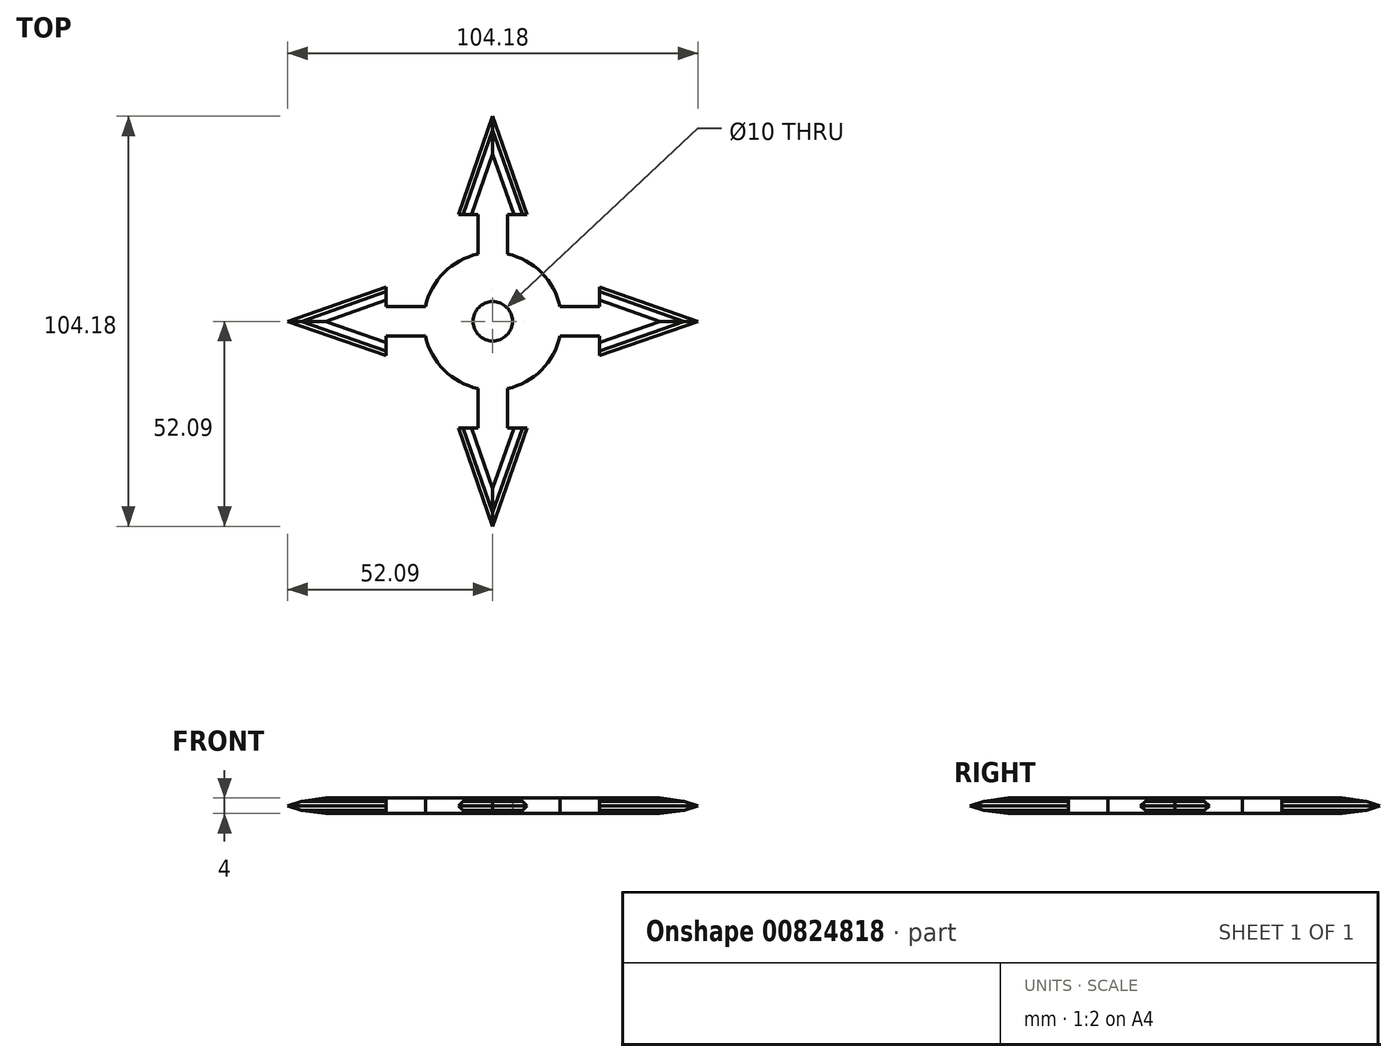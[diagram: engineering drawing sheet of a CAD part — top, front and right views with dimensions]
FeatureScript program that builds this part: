
annotation { "Feature Type Name" : "Feature", "Feature Type Description" : "" }
export const myFeature = defineFeature(function(context is Context, id is Id, definition is map)
    precondition{}
    {
        {
            var Q0;
            Q0=qCreatedBy(makeId("Top.planeOp"),FACE);
            var sketch = newSketch(context, id + "F0", { "sketchPlane" : qUnion([Q0])});
            skCircle(sketch, "E0", {"center": v(0, 0) * mm, "radius": 5 * mm});
            skCircle(sketch, "E1", {"center": v(0, 0) * mm, "radius": 17.5 * mm});
            skLineSegment(sketch, "E2", {"start": v(-3.75, 17.1) * mm, "end": v(-3.75, 27.1) * mm});
            skLineSegment(sketch, "E3", {"start": v(-3.75, 27.1) * mm, "end": v(3.75, 27.1) * mm});
            skLineSegment(sketch, "E4", {"start": v(3.75, 27.1) * mm, "end": v(3.75, 17.1) * mm});
            skLineSegment(sketch, "E5", {"start": v(17.1, 3.75) * mm, "end": v(27.1, 3.75) * mm});
            skLineSegment(sketch, "E6", {"start": v(27.1, 3.75) * mm, "end": v(27.1, -3.75) * mm});
            skLineSegment(sketch, "E7", {"start": v(27.1, -3.75) * mm, "end": v(17.1, -3.75) * mm});
            skLineSegment(sketch, "E8", {"start": v(3.75, -17.1) * mm, "end": v(3.75, -27.1) * mm});
            skLineSegment(sketch, "E9", {"start": v(3.75, -27.1) * mm, "end": v(-3.75, -27.1) * mm});
            skLineSegment(sketch, "E10", {"start": v(-3.75, -27.1) * mm, "end": v(-3.75, -17.1) * mm});
            skLineSegment(sketch, "E11", {"start": v(-17.1, 3.75) * mm, "end": v(-27.1, 3.75) * mm});
            skLineSegment(sketch, "E12", {"start": v(-27.1, 3.75) * mm, "end": v(-27.1, -3.75) * mm});
            skLineSegment(sketch, "E13", {"start": v(-27.1, -3.75) * mm, "end": v(-17.1, -3.75) * mm});
            skLineSegment(sketch, "E14", {"start": v(-27.1, 3.75) * mm, "end": v(-27.1, 8.75) * mm});
            skLineSegment(sketch, "E15", {"start": v(-27.1, 8.75) * mm, "end": v(-52.1, 0) * mm});
            skLineSegment(sketch, "E16", {"start": v(-52.1, 0) * mm, "end": v(-27.1, -8.75) * mm});
            skLineSegment(sketch, "E17", {"start": v(-27.1, -8.75) * mm, "end": v(-27.1, -3.75) * mm});
            skLineSegment(sketch, "E18", {"start": v(-3.75, 27.1) * mm, "end": v(-8.75, 27.1) * mm});
            skLineSegment(sketch, "E19", {"start": v(-8.75, 27.1) * mm, "end": v(0, 52.1) * mm});
            skLineSegment(sketch, "E20", {"start": v(0, 52.1) * mm, "end": v(8.75, 27.1) * mm});
            skLineSegment(sketch, "E21", {"start": v(8.75, 27.1) * mm, "end": v(3.75, 27.1) * mm});
            skLineSegment(sketch, "E22", {"start": v(27.1, 3.75) * mm, "end": v(27.1, 8.75) * mm});
            skLineSegment(sketch, "E23", {"start": v(27.1, 8.75) * mm, "end": v(52.1, 0) * mm});
            skLineSegment(sketch, "E24", {"start": v(52.1, 0) * mm, "end": v(27.1, -8.75) * mm});
            skLineSegment(sketch, "E25", {"start": v(27.1, -8.75) * mm, "end": v(27.1, -3.75) * mm});
            skLineSegment(sketch, "E26", {"start": v(3.75, -27.1) * mm, "end": v(8.75, -27.1) * mm});
            skLineSegment(sketch, "E27", {"start": v(8.75, -27.1) * mm, "end": v(0, -52.1) * mm});
            skLineSegment(sketch, "E28", {"start": v(0, -52.1) * mm, "end": v(-8.75, -27.1) * mm});
            skLineSegment(sketch, "E29", {"start": v(-8.75, -27.1) * mm, "end": v(-3.75, -27.1) * mm});
            skSolve(sketch);
        }
        {
            var Q0;
            Q0=makeQuery(id+"F0.imprint","IMPRINT",FACE,{"disambiguationData":[TD([[makeQuery(id+"F0.imprint","IMPRINT",EDGE,{"derivedFrom":sQuery(id+"F0.wireOp",EDGE,"E0")}),-1.0]])]});
            var Q1;
            {var subQ0=sQuery(id+"F0.wireOp",EDGE,"E11");Q1=makeQuery(id+"F0.imprint","IMPRINT",FACE,{"disambiguationData":[TD([[makeQuery(id+"F0.imprint","IMPRINT",EDGE,{"derivedFrom":subQ0}),1.0]])]});}
            var Q2;
            Q2=makeQuery(id+"F0.imprint","IMPRINT",FACE,{"disambiguationData":[TD([[makeQuery(id+"F0.imprint","IMPRINT",EDGE,{"derivedFrom":sQuery(id+"F0.wireOp",EDGE,"E12")}),-1.0]])]});
            var Q3;
            {var subQ0=sQuery(id+"F0.wireOp",EDGE,"E2");Q3=makeQuery(id+"F0.imprint","IMPRINT",FACE,{"disambiguationData":[TD([[makeQuery(id+"F0.imprint","IMPRINT",EDGE,{"derivedFrom":subQ0}),-1.0]])]});}
            var Q4;
            Q4=makeQuery(id+"F0.imprint","IMPRINT",FACE,{"disambiguationData":[TD([[makeQuery(id+"F0.imprint","IMPRINT",EDGE,{"derivedFrom":sQuery(id+"F0.wireOp",EDGE,"E3")}),1.0]])]});
            var Q5;
            Q5=makeQuery(id+"F0.imprint","IMPRINT",FACE,{"disambiguationData":[TD([[makeQuery(id+"F0.imprint","IMPRINT",EDGE,{"derivedFrom":sQuery(id+"F0.wireOp",EDGE,"E6")}),1.0]])]});
            var Q6;
            Q6=makeQuery(id+"F0.imprint","IMPRINT",FACE,{"disambiguationData":[TD([[makeQuery(id+"F0.imprint","IMPRINT",EDGE,{"derivedFrom":sQuery(id+"F0.wireOp",EDGE,"E9")}),1.0]])]});
            var Q7;
            {var subQ0=sQuery(id+"F0.wireOp",EDGE,"E8");Q7=makeQuery(id+"F0.imprint","IMPRINT",FACE,{"disambiguationData":[TD([[makeQuery(id+"F0.imprint","IMPRINT",EDGE,{"derivedFrom":subQ0}),-1.0]])]});}
            var Q8;
            {var subQ0=sQuery(id+"F0.wireOp",EDGE,"E5");Q8=makeQuery(id+"F0.imprint","IMPRINT",FACE,{"disambiguationData":[TD([[makeQuery(id+"F0.imprint","IMPRINT",EDGE,{"derivedFrom":subQ0}),-1.0]])]});}
            extrude(context, id + "F1", {"entities" : qUnion([Q0, Q1, Q2, Q3, Q4, Q5, Q6, Q7, Q8]), "endBound" : BoundingType.SYMMETRIC, "depth" : 4 * mm, "offsetDistance" : 25 * mm});
        }
        {
            var Q0;
            Q0=makeQuery(id+"F1.opExtrude","CAP_EDGE",EDGE,{"disambiguationData":[OSD([sQuery(id+"F0.wireOp",EDGE,"E27")])],"isStart":false});
            var Q1;
            Q1=makeQuery(id+"F1.opExtrude","CAP_EDGE",EDGE,{"disambiguationData":[OSD([sQuery(id+"F0.wireOp",EDGE,"E28")])],"isStart":false});
            var Q2;
            Q2=makeQuery(id+"F1.opExtrude","CAP_EDGE",EDGE,{"disambiguationData":[OSD([sQuery(id+"F0.wireOp",EDGE,"E27")])],"isStart":true});
            var Q3;
            Q3=makeQuery(id+"F1.opExtrude","CAP_EDGE",EDGE,{"disambiguationData":[OSD([sQuery(id+"F0.wireOp",EDGE,"E28")])],"isStart":true});
            var Q4;
            Q4=makeQuery(id+"F1.opExtrude","CAP_EDGE",EDGE,{"disambiguationData":[OSD([sQuery(id+"F0.wireOp",EDGE,"E24")])],"isStart":true});
            var Q5;
            Q5=makeQuery(id+"F1.opExtrude","CAP_EDGE",EDGE,{"disambiguationData":[OSD([sQuery(id+"F0.wireOp",EDGE,"E24")])],"isStart":false});
            var Q6;
            Q6=makeQuery(id+"F1.opExtrude","CAP_EDGE",EDGE,{"disambiguationData":[OSD([sQuery(id+"F0.wireOp",EDGE,"E23")])],"isStart":false});
            var Q7;
            Q7=makeQuery(id+"F1.opExtrude","CAP_EDGE",EDGE,{"disambiguationData":[OSD([sQuery(id+"F0.wireOp",EDGE,"E16")])],"isStart":false});
            var Q8;
            Q8=makeQuery(id+"F1.opExtrude","CAP_EDGE",EDGE,{"disambiguationData":[OSD([sQuery(id+"F0.wireOp",EDGE,"E16")])],"isStart":true});
            var Q9;
            Q9=makeQuery(id+"F1.opExtrude","CAP_EDGE",EDGE,{"disambiguationData":[OSD([sQuery(id+"F0.wireOp",EDGE,"E19")])],"isStart":false});
            var Q10;
            Q10=makeQuery(id+"F1.opExtrude","CAP_EDGE",EDGE,{"disambiguationData":[OSD([sQuery(id+"F0.wireOp",EDGE,"E20")])],"isStart":false});
            var Q11;
            Q11=makeQuery(id+"F1.opExtrude","CAP_EDGE",EDGE,{"disambiguationData":[OSD([sQuery(id+"F0.wireOp",EDGE,"E23")])],"isStart":true});
            var Q12;
            Q12=makeQuery(id+"F1.opExtrude","CAP_EDGE",EDGE,{"disambiguationData":[OSD([sQuery(id+"F0.wireOp",EDGE,"E20")])],"isStart":true});
            var Q13;
            Q13=makeQuery(id+"F1.opExtrude","CAP_EDGE",EDGE,{"disambiguationData":[OSD([sQuery(id+"F0.wireOp",EDGE,"E15")])],"isStart":false});
            var Q14;
            Q14=makeQuery(id+"F1.opExtrude","CAP_EDGE",EDGE,{"disambiguationData":[OSD([sQuery(id+"F0.wireOp",EDGE,"E15")])],"isStart":true});
            var Q15;
            Q15=makeQuery(id+"F1.opExtrude","CAP_EDGE",EDGE,{"disambiguationData":[OSD([sQuery(id+"F0.wireOp",EDGE,"E19")])],"isStart":true});
            chamfer(context, id + "F2", {"entities" : qUnion([Q0, Q1, Q2, Q3, Q4, Q5, Q6, Q7, Q8, Q9, Q10, Q11, Q12, Q13, Q14, Q15]), "width" : 2 * mm, "tangentPropagation" : true});
        }
        {
            var Q0;
            {var subQ0=sQuery(id+"F0.wireOp",EDGE,"E27");Q0=makeQuery(id+"F2.opChamfer","BLEND_EDGE",EDGE,{"blendedFrom":[makeQuery(id+"F1.opExtrude","CAP_EDGE",EDGE,{"disambiguationData":[OSD([subQ0])],"isStart":false}),makeQuery(id+"F1.opExtrude","CAP_FACE",FACE,{"disambiguationData":[OSD([sQuery(id+"F0.wireOp",EDGE,"E0"),sQuery(id+"F0.wireOp",EDGE,"E1"),sQuery(id+"F0.wireOp",EDGE,"E2"),sQuery(id+"F0.wireOp",EDGE,"E4"),sQuery(id+"F0.wireOp",EDGE,"E5"),sQuery(id+"F0.wireOp",EDGE,"E7"),sQuery(id+"F0.wireOp",EDGE,"E8"),sQuery(id+"F0.wireOp",EDGE,"E10"),sQuery(id+"F0.wireOp",EDGE,"E11"),sQuery(id+"F0.wireOp",EDGE,"E13"),sQuery(id+"F0.wireOp",EDGE,"E14"),sQuery(id+"F0.wireOp",EDGE,"E15"),sQuery(id+"F0.wireOp",EDGE,"E16"),sQuery(id+"F0.wireOp",EDGE,"E17"),sQuery(id+"F0.wireOp",EDGE,"E18"),sQuery(id+"F0.wireOp",EDGE,"E19"),sQuery(id+"F0.wireOp",EDGE,"E20"),sQuery(id+"F0.wireOp",EDGE,"E21"),sQuery(id+"F0.wireOp",EDGE,"E22"),sQuery(id+"F0.wireOp",EDGE,"E23"),sQuery(id+"F0.wireOp",EDGE,"E24"),sQuery(id+"F0.wireOp",EDGE,"E25"),sQuery(id+"F0.wireOp",EDGE,"E26"),subQ0,sQuery(id+"F0.wireOp",EDGE,"E28"),sQuery(id+"F0.wireOp",EDGE,"E29")])],"isStart":false})],"blendedInto":[makeQuery(id+"F1.opExtrude","CAP_FACE",FACE,{"disambiguationData":[OSD([sQuery(id+"F0.wireOp",EDGE,"E0"),sQuery(id+"F0.wireOp",EDGE,"E1"),sQuery(id+"F0.wireOp",EDGE,"E2"),sQuery(id+"F0.wireOp",EDGE,"E4"),sQuery(id+"F0.wireOp",EDGE,"E5"),sQuery(id+"F0.wireOp",EDGE,"E7"),sQuery(id+"F0.wireOp",EDGE,"E8"),sQuery(id+"F0.wireOp",EDGE,"E10"),sQuery(id+"F0.wireOp",EDGE,"E11"),sQuery(id+"F0.wireOp",EDGE,"E13"),sQuery(id+"F0.wireOp",EDGE,"E14"),sQuery(id+"F0.wireOp",EDGE,"E15"),sQuery(id+"F0.wireOp",EDGE,"E16"),sQuery(id+"F0.wireOp",EDGE,"E17"),sQuery(id+"F0.wireOp",EDGE,"E18"),sQuery(id+"F0.wireOp",EDGE,"E19"),sQuery(id+"F0.wireOp",EDGE,"E20"),sQuery(id+"F0.wireOp",EDGE,"E21"),sQuery(id+"F0.wireOp",EDGE,"E22"),sQuery(id+"F0.wireOp",EDGE,"E23"),sQuery(id+"F0.wireOp",EDGE,"E24"),sQuery(id+"F0.wireOp",EDGE,"E25"),sQuery(id+"F0.wireOp",EDGE,"E26"),subQ0,sQuery(id+"F0.wireOp",EDGE,"E28"),sQuery(id+"F0.wireOp",EDGE,"E29")])],"isStart":false})]});}
            var Q1;
            {var subQ0=sQuery(id+"F0.wireOp",EDGE,"E28");Q1=makeQuery(id+"F2.opChamfer","BLEND_EDGE",EDGE,{"blendedFrom":[makeQuery(id+"F1.opExtrude","CAP_EDGE",EDGE,{"disambiguationData":[OSD([subQ0])],"isStart":false}),makeQuery(id+"F1.opExtrude","CAP_FACE",FACE,{"disambiguationData":[OSD([sQuery(id+"F0.wireOp",EDGE,"E0"),sQuery(id+"F0.wireOp",EDGE,"E1"),sQuery(id+"F0.wireOp",EDGE,"E2"),sQuery(id+"F0.wireOp",EDGE,"E4"),sQuery(id+"F0.wireOp",EDGE,"E5"),sQuery(id+"F0.wireOp",EDGE,"E7"),sQuery(id+"F0.wireOp",EDGE,"E8"),sQuery(id+"F0.wireOp",EDGE,"E10"),sQuery(id+"F0.wireOp",EDGE,"E11"),sQuery(id+"F0.wireOp",EDGE,"E13"),sQuery(id+"F0.wireOp",EDGE,"E14"),sQuery(id+"F0.wireOp",EDGE,"E15"),sQuery(id+"F0.wireOp",EDGE,"E16"),sQuery(id+"F0.wireOp",EDGE,"E17"),sQuery(id+"F0.wireOp",EDGE,"E18"),sQuery(id+"F0.wireOp",EDGE,"E19"),sQuery(id+"F0.wireOp",EDGE,"E20"),sQuery(id+"F0.wireOp",EDGE,"E21"),sQuery(id+"F0.wireOp",EDGE,"E22"),sQuery(id+"F0.wireOp",EDGE,"E23"),sQuery(id+"F0.wireOp",EDGE,"E24"),sQuery(id+"F0.wireOp",EDGE,"E25"),sQuery(id+"F0.wireOp",EDGE,"E26"),sQuery(id+"F0.wireOp",EDGE,"E27"),subQ0,sQuery(id+"F0.wireOp",EDGE,"E29")])],"isStart":false})],"blendedInto":[makeQuery(id+"F1.opExtrude","CAP_FACE",FACE,{"disambiguationData":[OSD([sQuery(id+"F0.wireOp",EDGE,"E0"),sQuery(id+"F0.wireOp",EDGE,"E1"),sQuery(id+"F0.wireOp",EDGE,"E2"),sQuery(id+"F0.wireOp",EDGE,"E4"),sQuery(id+"F0.wireOp",EDGE,"E5"),sQuery(id+"F0.wireOp",EDGE,"E7"),sQuery(id+"F0.wireOp",EDGE,"E8"),sQuery(id+"F0.wireOp",EDGE,"E10"),sQuery(id+"F0.wireOp",EDGE,"E11"),sQuery(id+"F0.wireOp",EDGE,"E13"),sQuery(id+"F0.wireOp",EDGE,"E14"),sQuery(id+"F0.wireOp",EDGE,"E15"),sQuery(id+"F0.wireOp",EDGE,"E16"),sQuery(id+"F0.wireOp",EDGE,"E17"),sQuery(id+"F0.wireOp",EDGE,"E18"),sQuery(id+"F0.wireOp",EDGE,"E19"),sQuery(id+"F0.wireOp",EDGE,"E20"),sQuery(id+"F0.wireOp",EDGE,"E21"),sQuery(id+"F0.wireOp",EDGE,"E22"),sQuery(id+"F0.wireOp",EDGE,"E23"),sQuery(id+"F0.wireOp",EDGE,"E24"),sQuery(id+"F0.wireOp",EDGE,"E25"),sQuery(id+"F0.wireOp",EDGE,"E26"),sQuery(id+"F0.wireOp",EDGE,"E27"),subQ0,sQuery(id+"F0.wireOp",EDGE,"E29")])],"isStart":false})]});}
            var Q2;
            {var subQ0=sQuery(id+"F0.wireOp",EDGE,"E27");Q2=makeQuery(id+"F2.opChamfer","BLEND_EDGE",EDGE,{"blendedFrom":[makeQuery(id+"F1.opExtrude","CAP_EDGE",EDGE,{"disambiguationData":[OSD([subQ0])],"isStart":true}),makeQuery(id+"F1.opExtrude","CAP_FACE",FACE,{"disambiguationData":[OSD([sQuery(id+"F0.wireOp",EDGE,"E0"),sQuery(id+"F0.wireOp",EDGE,"E1"),sQuery(id+"F0.wireOp",EDGE,"E2"),sQuery(id+"F0.wireOp",EDGE,"E4"),sQuery(id+"F0.wireOp",EDGE,"E5"),sQuery(id+"F0.wireOp",EDGE,"E7"),sQuery(id+"F0.wireOp",EDGE,"E8"),sQuery(id+"F0.wireOp",EDGE,"E10"),sQuery(id+"F0.wireOp",EDGE,"E11"),sQuery(id+"F0.wireOp",EDGE,"E13"),sQuery(id+"F0.wireOp",EDGE,"E14"),sQuery(id+"F0.wireOp",EDGE,"E15"),sQuery(id+"F0.wireOp",EDGE,"E16"),sQuery(id+"F0.wireOp",EDGE,"E17"),sQuery(id+"F0.wireOp",EDGE,"E18"),sQuery(id+"F0.wireOp",EDGE,"E19"),sQuery(id+"F0.wireOp",EDGE,"E20"),sQuery(id+"F0.wireOp",EDGE,"E21"),sQuery(id+"F0.wireOp",EDGE,"E22"),sQuery(id+"F0.wireOp",EDGE,"E23"),sQuery(id+"F0.wireOp",EDGE,"E24"),sQuery(id+"F0.wireOp",EDGE,"E25"),sQuery(id+"F0.wireOp",EDGE,"E26"),subQ0,sQuery(id+"F0.wireOp",EDGE,"E28"),sQuery(id+"F0.wireOp",EDGE,"E29")])],"isStart":true})],"blendedInto":[makeQuery(id+"F1.opExtrude","CAP_FACE",FACE,{"disambiguationData":[OSD([sQuery(id+"F0.wireOp",EDGE,"E0"),sQuery(id+"F0.wireOp",EDGE,"E1"),sQuery(id+"F0.wireOp",EDGE,"E2"),sQuery(id+"F0.wireOp",EDGE,"E4"),sQuery(id+"F0.wireOp",EDGE,"E5"),sQuery(id+"F0.wireOp",EDGE,"E7"),sQuery(id+"F0.wireOp",EDGE,"E8"),sQuery(id+"F0.wireOp",EDGE,"E10"),sQuery(id+"F0.wireOp",EDGE,"E11"),sQuery(id+"F0.wireOp",EDGE,"E13"),sQuery(id+"F0.wireOp",EDGE,"E14"),sQuery(id+"F0.wireOp",EDGE,"E15"),sQuery(id+"F0.wireOp",EDGE,"E16"),sQuery(id+"F0.wireOp",EDGE,"E17"),sQuery(id+"F0.wireOp",EDGE,"E18"),sQuery(id+"F0.wireOp",EDGE,"E19"),sQuery(id+"F0.wireOp",EDGE,"E20"),sQuery(id+"F0.wireOp",EDGE,"E21"),sQuery(id+"F0.wireOp",EDGE,"E22"),sQuery(id+"F0.wireOp",EDGE,"E23"),sQuery(id+"F0.wireOp",EDGE,"E24"),sQuery(id+"F0.wireOp",EDGE,"E25"),sQuery(id+"F0.wireOp",EDGE,"E26"),subQ0,sQuery(id+"F0.wireOp",EDGE,"E28"),sQuery(id+"F0.wireOp",EDGE,"E29")])],"isStart":true})]});}
            var Q3;
            {var subQ0=sQuery(id+"F0.wireOp",EDGE,"E28");Q3=makeQuery(id+"F2.opChamfer","BLEND_EDGE",EDGE,{"blendedFrom":[makeQuery(id+"F1.opExtrude","CAP_EDGE",EDGE,{"disambiguationData":[OSD([subQ0])],"isStart":true}),makeQuery(id+"F1.opExtrude","CAP_FACE",FACE,{"disambiguationData":[OSD([sQuery(id+"F0.wireOp",EDGE,"E0"),sQuery(id+"F0.wireOp",EDGE,"E1"),sQuery(id+"F0.wireOp",EDGE,"E2"),sQuery(id+"F0.wireOp",EDGE,"E4"),sQuery(id+"F0.wireOp",EDGE,"E5"),sQuery(id+"F0.wireOp",EDGE,"E7"),sQuery(id+"F0.wireOp",EDGE,"E8"),sQuery(id+"F0.wireOp",EDGE,"E10"),sQuery(id+"F0.wireOp",EDGE,"E11"),sQuery(id+"F0.wireOp",EDGE,"E13"),sQuery(id+"F0.wireOp",EDGE,"E14"),sQuery(id+"F0.wireOp",EDGE,"E15"),sQuery(id+"F0.wireOp",EDGE,"E16"),sQuery(id+"F0.wireOp",EDGE,"E17"),sQuery(id+"F0.wireOp",EDGE,"E18"),sQuery(id+"F0.wireOp",EDGE,"E19"),sQuery(id+"F0.wireOp",EDGE,"E20"),sQuery(id+"F0.wireOp",EDGE,"E21"),sQuery(id+"F0.wireOp",EDGE,"E22"),sQuery(id+"F0.wireOp",EDGE,"E23"),sQuery(id+"F0.wireOp",EDGE,"E24"),sQuery(id+"F0.wireOp",EDGE,"E25"),sQuery(id+"F0.wireOp",EDGE,"E26"),sQuery(id+"F0.wireOp",EDGE,"E27"),subQ0,sQuery(id+"F0.wireOp",EDGE,"E29")])],"isStart":true})],"blendedInto":[makeQuery(id+"F1.opExtrude","CAP_FACE",FACE,{"disambiguationData":[OSD([sQuery(id+"F0.wireOp",EDGE,"E0"),sQuery(id+"F0.wireOp",EDGE,"E1"),sQuery(id+"F0.wireOp",EDGE,"E2"),sQuery(id+"F0.wireOp",EDGE,"E4"),sQuery(id+"F0.wireOp",EDGE,"E5"),sQuery(id+"F0.wireOp",EDGE,"E7"),sQuery(id+"F0.wireOp",EDGE,"E8"),sQuery(id+"F0.wireOp",EDGE,"E10"),sQuery(id+"F0.wireOp",EDGE,"E11"),sQuery(id+"F0.wireOp",EDGE,"E13"),sQuery(id+"F0.wireOp",EDGE,"E14"),sQuery(id+"F0.wireOp",EDGE,"E15"),sQuery(id+"F0.wireOp",EDGE,"E16"),sQuery(id+"F0.wireOp",EDGE,"E17"),sQuery(id+"F0.wireOp",EDGE,"E18"),sQuery(id+"F0.wireOp",EDGE,"E19"),sQuery(id+"F0.wireOp",EDGE,"E20"),sQuery(id+"F0.wireOp",EDGE,"E21"),sQuery(id+"F0.wireOp",EDGE,"E22"),sQuery(id+"F0.wireOp",EDGE,"E23"),sQuery(id+"F0.wireOp",EDGE,"E24"),sQuery(id+"F0.wireOp",EDGE,"E25"),sQuery(id+"F0.wireOp",EDGE,"E26"),sQuery(id+"F0.wireOp",EDGE,"E27"),subQ0,sQuery(id+"F0.wireOp",EDGE,"E29")])],"isStart":true})]});}
            var Q4;
            {var subQ0=sQuery(id+"F0.wireOp",EDGE,"E24");Q4=makeQuery(id+"F2.opChamfer","BLEND_EDGE",EDGE,{"blendedFrom":[makeQuery(id+"F1.opExtrude","CAP_EDGE",EDGE,{"disambiguationData":[OSD([subQ0])],"isStart":false}),makeQuery(id+"F1.opExtrude","CAP_FACE",FACE,{"disambiguationData":[OSD([sQuery(id+"F0.wireOp",EDGE,"E0"),sQuery(id+"F0.wireOp",EDGE,"E1"),sQuery(id+"F0.wireOp",EDGE,"E2"),sQuery(id+"F0.wireOp",EDGE,"E4"),sQuery(id+"F0.wireOp",EDGE,"E5"),sQuery(id+"F0.wireOp",EDGE,"E7"),sQuery(id+"F0.wireOp",EDGE,"E8"),sQuery(id+"F0.wireOp",EDGE,"E10"),sQuery(id+"F0.wireOp",EDGE,"E11"),sQuery(id+"F0.wireOp",EDGE,"E13"),sQuery(id+"F0.wireOp",EDGE,"E14"),sQuery(id+"F0.wireOp",EDGE,"E15"),sQuery(id+"F0.wireOp",EDGE,"E16"),sQuery(id+"F0.wireOp",EDGE,"E17"),sQuery(id+"F0.wireOp",EDGE,"E18"),sQuery(id+"F0.wireOp",EDGE,"E19"),sQuery(id+"F0.wireOp",EDGE,"E20"),sQuery(id+"F0.wireOp",EDGE,"E21"),sQuery(id+"F0.wireOp",EDGE,"E22"),sQuery(id+"F0.wireOp",EDGE,"E23"),subQ0,sQuery(id+"F0.wireOp",EDGE,"E25"),sQuery(id+"F0.wireOp",EDGE,"E26"),sQuery(id+"F0.wireOp",EDGE,"E27"),sQuery(id+"F0.wireOp",EDGE,"E28"),sQuery(id+"F0.wireOp",EDGE,"E29")])],"isStart":false})],"blendedInto":[makeQuery(id+"F1.opExtrude","CAP_FACE",FACE,{"disambiguationData":[OSD([sQuery(id+"F0.wireOp",EDGE,"E0"),sQuery(id+"F0.wireOp",EDGE,"E1"),sQuery(id+"F0.wireOp",EDGE,"E2"),sQuery(id+"F0.wireOp",EDGE,"E4"),sQuery(id+"F0.wireOp",EDGE,"E5"),sQuery(id+"F0.wireOp",EDGE,"E7"),sQuery(id+"F0.wireOp",EDGE,"E8"),sQuery(id+"F0.wireOp",EDGE,"E10"),sQuery(id+"F0.wireOp",EDGE,"E11"),sQuery(id+"F0.wireOp",EDGE,"E13"),sQuery(id+"F0.wireOp",EDGE,"E14"),sQuery(id+"F0.wireOp",EDGE,"E15"),sQuery(id+"F0.wireOp",EDGE,"E16"),sQuery(id+"F0.wireOp",EDGE,"E17"),sQuery(id+"F0.wireOp",EDGE,"E18"),sQuery(id+"F0.wireOp",EDGE,"E19"),sQuery(id+"F0.wireOp",EDGE,"E20"),sQuery(id+"F0.wireOp",EDGE,"E21"),sQuery(id+"F0.wireOp",EDGE,"E22"),sQuery(id+"F0.wireOp",EDGE,"E23"),subQ0,sQuery(id+"F0.wireOp",EDGE,"E25"),sQuery(id+"F0.wireOp",EDGE,"E26"),sQuery(id+"F0.wireOp",EDGE,"E27"),sQuery(id+"F0.wireOp",EDGE,"E28"),sQuery(id+"F0.wireOp",EDGE,"E29")])],"isStart":false})]});}
            var Q5;
            {var subQ0=sQuery(id+"F0.wireOp",EDGE,"E23");Q5=makeQuery(id+"F2.opChamfer","BLEND_EDGE",EDGE,{"blendedFrom":[makeQuery(id+"F1.opExtrude","CAP_EDGE",EDGE,{"disambiguationData":[OSD([subQ0])],"isStart":false}),makeQuery(id+"F1.opExtrude","CAP_FACE",FACE,{"disambiguationData":[OSD([sQuery(id+"F0.wireOp",EDGE,"E0"),sQuery(id+"F0.wireOp",EDGE,"E1"),sQuery(id+"F0.wireOp",EDGE,"E2"),sQuery(id+"F0.wireOp",EDGE,"E4"),sQuery(id+"F0.wireOp",EDGE,"E5"),sQuery(id+"F0.wireOp",EDGE,"E7"),sQuery(id+"F0.wireOp",EDGE,"E8"),sQuery(id+"F0.wireOp",EDGE,"E10"),sQuery(id+"F0.wireOp",EDGE,"E11"),sQuery(id+"F0.wireOp",EDGE,"E13"),sQuery(id+"F0.wireOp",EDGE,"E14"),sQuery(id+"F0.wireOp",EDGE,"E15"),sQuery(id+"F0.wireOp",EDGE,"E16"),sQuery(id+"F0.wireOp",EDGE,"E17"),sQuery(id+"F0.wireOp",EDGE,"E18"),sQuery(id+"F0.wireOp",EDGE,"E19"),sQuery(id+"F0.wireOp",EDGE,"E20"),sQuery(id+"F0.wireOp",EDGE,"E21"),sQuery(id+"F0.wireOp",EDGE,"E22"),subQ0,sQuery(id+"F0.wireOp",EDGE,"E24"),sQuery(id+"F0.wireOp",EDGE,"E25"),sQuery(id+"F0.wireOp",EDGE,"E26"),sQuery(id+"F0.wireOp",EDGE,"E27"),sQuery(id+"F0.wireOp",EDGE,"E28"),sQuery(id+"F0.wireOp",EDGE,"E29")])],"isStart":false})],"blendedInto":[makeQuery(id+"F1.opExtrude","CAP_FACE",FACE,{"disambiguationData":[OSD([sQuery(id+"F0.wireOp",EDGE,"E0"),sQuery(id+"F0.wireOp",EDGE,"E1"),sQuery(id+"F0.wireOp",EDGE,"E2"),sQuery(id+"F0.wireOp",EDGE,"E4"),sQuery(id+"F0.wireOp",EDGE,"E5"),sQuery(id+"F0.wireOp",EDGE,"E7"),sQuery(id+"F0.wireOp",EDGE,"E8"),sQuery(id+"F0.wireOp",EDGE,"E10"),sQuery(id+"F0.wireOp",EDGE,"E11"),sQuery(id+"F0.wireOp",EDGE,"E13"),sQuery(id+"F0.wireOp",EDGE,"E14"),sQuery(id+"F0.wireOp",EDGE,"E15"),sQuery(id+"F0.wireOp",EDGE,"E16"),sQuery(id+"F0.wireOp",EDGE,"E17"),sQuery(id+"F0.wireOp",EDGE,"E18"),sQuery(id+"F0.wireOp",EDGE,"E19"),sQuery(id+"F0.wireOp",EDGE,"E20"),sQuery(id+"F0.wireOp",EDGE,"E21"),sQuery(id+"F0.wireOp",EDGE,"E22"),subQ0,sQuery(id+"F0.wireOp",EDGE,"E24"),sQuery(id+"F0.wireOp",EDGE,"E25"),sQuery(id+"F0.wireOp",EDGE,"E26"),sQuery(id+"F0.wireOp",EDGE,"E27"),sQuery(id+"F0.wireOp",EDGE,"E28"),sQuery(id+"F0.wireOp",EDGE,"E29")])],"isStart":false})]});}
            var Q6;
            {var subQ0=sQuery(id+"F0.wireOp",EDGE,"E20");Q6=makeQuery(id+"F2.opChamfer","BLEND_EDGE",EDGE,{"blendedFrom":[makeQuery(id+"F1.opExtrude","CAP_EDGE",EDGE,{"disambiguationData":[OSD([subQ0])],"isStart":false}),makeQuery(id+"F1.opExtrude","CAP_FACE",FACE,{"disambiguationData":[OSD([sQuery(id+"F0.wireOp",EDGE,"E0"),sQuery(id+"F0.wireOp",EDGE,"E1"),sQuery(id+"F0.wireOp",EDGE,"E2"),sQuery(id+"F0.wireOp",EDGE,"E4"),sQuery(id+"F0.wireOp",EDGE,"E5"),sQuery(id+"F0.wireOp",EDGE,"E7"),sQuery(id+"F0.wireOp",EDGE,"E8"),sQuery(id+"F0.wireOp",EDGE,"E10"),sQuery(id+"F0.wireOp",EDGE,"E11"),sQuery(id+"F0.wireOp",EDGE,"E13"),sQuery(id+"F0.wireOp",EDGE,"E14"),sQuery(id+"F0.wireOp",EDGE,"E15"),sQuery(id+"F0.wireOp",EDGE,"E16"),sQuery(id+"F0.wireOp",EDGE,"E17"),sQuery(id+"F0.wireOp",EDGE,"E18"),sQuery(id+"F0.wireOp",EDGE,"E19"),subQ0,sQuery(id+"F0.wireOp",EDGE,"E21"),sQuery(id+"F0.wireOp",EDGE,"E22"),sQuery(id+"F0.wireOp",EDGE,"E23"),sQuery(id+"F0.wireOp",EDGE,"E24"),sQuery(id+"F0.wireOp",EDGE,"E25"),sQuery(id+"F0.wireOp",EDGE,"E26"),sQuery(id+"F0.wireOp",EDGE,"E27"),sQuery(id+"F0.wireOp",EDGE,"E28"),sQuery(id+"F0.wireOp",EDGE,"E29")])],"isStart":false})],"blendedInto":[makeQuery(id+"F1.opExtrude","CAP_FACE",FACE,{"disambiguationData":[OSD([sQuery(id+"F0.wireOp",EDGE,"E0"),sQuery(id+"F0.wireOp",EDGE,"E1"),sQuery(id+"F0.wireOp",EDGE,"E2"),sQuery(id+"F0.wireOp",EDGE,"E4"),sQuery(id+"F0.wireOp",EDGE,"E5"),sQuery(id+"F0.wireOp",EDGE,"E7"),sQuery(id+"F0.wireOp",EDGE,"E8"),sQuery(id+"F0.wireOp",EDGE,"E10"),sQuery(id+"F0.wireOp",EDGE,"E11"),sQuery(id+"F0.wireOp",EDGE,"E13"),sQuery(id+"F0.wireOp",EDGE,"E14"),sQuery(id+"F0.wireOp",EDGE,"E15"),sQuery(id+"F0.wireOp",EDGE,"E16"),sQuery(id+"F0.wireOp",EDGE,"E17"),sQuery(id+"F0.wireOp",EDGE,"E18"),sQuery(id+"F0.wireOp",EDGE,"E19"),subQ0,sQuery(id+"F0.wireOp",EDGE,"E21"),sQuery(id+"F0.wireOp",EDGE,"E22"),sQuery(id+"F0.wireOp",EDGE,"E23"),sQuery(id+"F0.wireOp",EDGE,"E24"),sQuery(id+"F0.wireOp",EDGE,"E25"),sQuery(id+"F0.wireOp",EDGE,"E26"),sQuery(id+"F0.wireOp",EDGE,"E27"),sQuery(id+"F0.wireOp",EDGE,"E28"),sQuery(id+"F0.wireOp",EDGE,"E29")])],"isStart":false})]});}
            var Q7;
            {var subQ0=sQuery(id+"F0.wireOp",EDGE,"E19");Q7=makeQuery(id+"F2.opChamfer","BLEND_EDGE",EDGE,{"blendedFrom":[makeQuery(id+"F1.opExtrude","CAP_EDGE",EDGE,{"disambiguationData":[OSD([subQ0])],"isStart":false}),makeQuery(id+"F1.opExtrude","CAP_FACE",FACE,{"disambiguationData":[OSD([sQuery(id+"F0.wireOp",EDGE,"E0"),sQuery(id+"F0.wireOp",EDGE,"E1"),sQuery(id+"F0.wireOp",EDGE,"E2"),sQuery(id+"F0.wireOp",EDGE,"E4"),sQuery(id+"F0.wireOp",EDGE,"E5"),sQuery(id+"F0.wireOp",EDGE,"E7"),sQuery(id+"F0.wireOp",EDGE,"E8"),sQuery(id+"F0.wireOp",EDGE,"E10"),sQuery(id+"F0.wireOp",EDGE,"E11"),sQuery(id+"F0.wireOp",EDGE,"E13"),sQuery(id+"F0.wireOp",EDGE,"E14"),sQuery(id+"F0.wireOp",EDGE,"E15"),sQuery(id+"F0.wireOp",EDGE,"E16"),sQuery(id+"F0.wireOp",EDGE,"E17"),sQuery(id+"F0.wireOp",EDGE,"E18"),subQ0,sQuery(id+"F0.wireOp",EDGE,"E20"),sQuery(id+"F0.wireOp",EDGE,"E21"),sQuery(id+"F0.wireOp",EDGE,"E22"),sQuery(id+"F0.wireOp",EDGE,"E23"),sQuery(id+"F0.wireOp",EDGE,"E24"),sQuery(id+"F0.wireOp",EDGE,"E25"),sQuery(id+"F0.wireOp",EDGE,"E26"),sQuery(id+"F0.wireOp",EDGE,"E27"),sQuery(id+"F0.wireOp",EDGE,"E28"),sQuery(id+"F0.wireOp",EDGE,"E29")])],"isStart":false})],"blendedInto":[makeQuery(id+"F1.opExtrude","CAP_FACE",FACE,{"disambiguationData":[OSD([sQuery(id+"F0.wireOp",EDGE,"E0"),sQuery(id+"F0.wireOp",EDGE,"E1"),sQuery(id+"F0.wireOp",EDGE,"E2"),sQuery(id+"F0.wireOp",EDGE,"E4"),sQuery(id+"F0.wireOp",EDGE,"E5"),sQuery(id+"F0.wireOp",EDGE,"E7"),sQuery(id+"F0.wireOp",EDGE,"E8"),sQuery(id+"F0.wireOp",EDGE,"E10"),sQuery(id+"F0.wireOp",EDGE,"E11"),sQuery(id+"F0.wireOp",EDGE,"E13"),sQuery(id+"F0.wireOp",EDGE,"E14"),sQuery(id+"F0.wireOp",EDGE,"E15"),sQuery(id+"F0.wireOp",EDGE,"E16"),sQuery(id+"F0.wireOp",EDGE,"E17"),sQuery(id+"F0.wireOp",EDGE,"E18"),subQ0,sQuery(id+"F0.wireOp",EDGE,"E20"),sQuery(id+"F0.wireOp",EDGE,"E21"),sQuery(id+"F0.wireOp",EDGE,"E22"),sQuery(id+"F0.wireOp",EDGE,"E23"),sQuery(id+"F0.wireOp",EDGE,"E24"),sQuery(id+"F0.wireOp",EDGE,"E25"),sQuery(id+"F0.wireOp",EDGE,"E26"),sQuery(id+"F0.wireOp",EDGE,"E27"),sQuery(id+"F0.wireOp",EDGE,"E28"),sQuery(id+"F0.wireOp",EDGE,"E29")])],"isStart":false})]});}
            var Q8;
            {var subQ0=sQuery(id+"F0.wireOp",EDGE,"E15");Q8=makeQuery(id+"F2.opChamfer","BLEND_EDGE",EDGE,{"blendedFrom":[makeQuery(id+"F1.opExtrude","CAP_EDGE",EDGE,{"disambiguationData":[OSD([subQ0])],"isStart":false}),makeQuery(id+"F1.opExtrude","CAP_FACE",FACE,{"disambiguationData":[OSD([sQuery(id+"F0.wireOp",EDGE,"E0"),sQuery(id+"F0.wireOp",EDGE,"E1"),sQuery(id+"F0.wireOp",EDGE,"E2"),sQuery(id+"F0.wireOp",EDGE,"E4"),sQuery(id+"F0.wireOp",EDGE,"E5"),sQuery(id+"F0.wireOp",EDGE,"E7"),sQuery(id+"F0.wireOp",EDGE,"E8"),sQuery(id+"F0.wireOp",EDGE,"E10"),sQuery(id+"F0.wireOp",EDGE,"E11"),sQuery(id+"F0.wireOp",EDGE,"E13"),sQuery(id+"F0.wireOp",EDGE,"E14"),subQ0,sQuery(id+"F0.wireOp",EDGE,"E16"),sQuery(id+"F0.wireOp",EDGE,"E17"),sQuery(id+"F0.wireOp",EDGE,"E18"),sQuery(id+"F0.wireOp",EDGE,"E19"),sQuery(id+"F0.wireOp",EDGE,"E20"),sQuery(id+"F0.wireOp",EDGE,"E21"),sQuery(id+"F0.wireOp",EDGE,"E22"),sQuery(id+"F0.wireOp",EDGE,"E23"),sQuery(id+"F0.wireOp",EDGE,"E24"),sQuery(id+"F0.wireOp",EDGE,"E25"),sQuery(id+"F0.wireOp",EDGE,"E26"),sQuery(id+"F0.wireOp",EDGE,"E27"),sQuery(id+"F0.wireOp",EDGE,"E28"),sQuery(id+"F0.wireOp",EDGE,"E29")])],"isStart":false})],"blendedInto":[makeQuery(id+"F1.opExtrude","CAP_FACE",FACE,{"disambiguationData":[OSD([sQuery(id+"F0.wireOp",EDGE,"E0"),sQuery(id+"F0.wireOp",EDGE,"E1"),sQuery(id+"F0.wireOp",EDGE,"E2"),sQuery(id+"F0.wireOp",EDGE,"E4"),sQuery(id+"F0.wireOp",EDGE,"E5"),sQuery(id+"F0.wireOp",EDGE,"E7"),sQuery(id+"F0.wireOp",EDGE,"E8"),sQuery(id+"F0.wireOp",EDGE,"E10"),sQuery(id+"F0.wireOp",EDGE,"E11"),sQuery(id+"F0.wireOp",EDGE,"E13"),sQuery(id+"F0.wireOp",EDGE,"E14"),subQ0,sQuery(id+"F0.wireOp",EDGE,"E16"),sQuery(id+"F0.wireOp",EDGE,"E17"),sQuery(id+"F0.wireOp",EDGE,"E18"),sQuery(id+"F0.wireOp",EDGE,"E19"),sQuery(id+"F0.wireOp",EDGE,"E20"),sQuery(id+"F0.wireOp",EDGE,"E21"),sQuery(id+"F0.wireOp",EDGE,"E22"),sQuery(id+"F0.wireOp",EDGE,"E23"),sQuery(id+"F0.wireOp",EDGE,"E24"),sQuery(id+"F0.wireOp",EDGE,"E25"),sQuery(id+"F0.wireOp",EDGE,"E26"),sQuery(id+"F0.wireOp",EDGE,"E27"),sQuery(id+"F0.wireOp",EDGE,"E28"),sQuery(id+"F0.wireOp",EDGE,"E29")])],"isStart":false})]});}
            var Q9;
            {var subQ0=sQuery(id+"F0.wireOp",EDGE,"E16");Q9=makeQuery(id+"F2.opChamfer","BLEND_EDGE",EDGE,{"blendedFrom":[makeQuery(id+"F1.opExtrude","CAP_EDGE",EDGE,{"disambiguationData":[OSD([subQ0])],"isStart":false}),makeQuery(id+"F1.opExtrude","CAP_FACE",FACE,{"disambiguationData":[OSD([sQuery(id+"F0.wireOp",EDGE,"E0"),sQuery(id+"F0.wireOp",EDGE,"E1"),sQuery(id+"F0.wireOp",EDGE,"E2"),sQuery(id+"F0.wireOp",EDGE,"E4"),sQuery(id+"F0.wireOp",EDGE,"E5"),sQuery(id+"F0.wireOp",EDGE,"E7"),sQuery(id+"F0.wireOp",EDGE,"E8"),sQuery(id+"F0.wireOp",EDGE,"E10"),sQuery(id+"F0.wireOp",EDGE,"E11"),sQuery(id+"F0.wireOp",EDGE,"E13"),sQuery(id+"F0.wireOp",EDGE,"E14"),sQuery(id+"F0.wireOp",EDGE,"E15"),subQ0,sQuery(id+"F0.wireOp",EDGE,"E17"),sQuery(id+"F0.wireOp",EDGE,"E18"),sQuery(id+"F0.wireOp",EDGE,"E19"),sQuery(id+"F0.wireOp",EDGE,"E20"),sQuery(id+"F0.wireOp",EDGE,"E21"),sQuery(id+"F0.wireOp",EDGE,"E22"),sQuery(id+"F0.wireOp",EDGE,"E23"),sQuery(id+"F0.wireOp",EDGE,"E24"),sQuery(id+"F0.wireOp",EDGE,"E25"),sQuery(id+"F0.wireOp",EDGE,"E26"),sQuery(id+"F0.wireOp",EDGE,"E27"),sQuery(id+"F0.wireOp",EDGE,"E28"),sQuery(id+"F0.wireOp",EDGE,"E29")])],"isStart":false})],"blendedInto":[makeQuery(id+"F1.opExtrude","CAP_FACE",FACE,{"disambiguationData":[OSD([sQuery(id+"F0.wireOp",EDGE,"E0"),sQuery(id+"F0.wireOp",EDGE,"E1"),sQuery(id+"F0.wireOp",EDGE,"E2"),sQuery(id+"F0.wireOp",EDGE,"E4"),sQuery(id+"F0.wireOp",EDGE,"E5"),sQuery(id+"F0.wireOp",EDGE,"E7"),sQuery(id+"F0.wireOp",EDGE,"E8"),sQuery(id+"F0.wireOp",EDGE,"E10"),sQuery(id+"F0.wireOp",EDGE,"E11"),sQuery(id+"F0.wireOp",EDGE,"E13"),sQuery(id+"F0.wireOp",EDGE,"E14"),sQuery(id+"F0.wireOp",EDGE,"E15"),subQ0,sQuery(id+"F0.wireOp",EDGE,"E17"),sQuery(id+"F0.wireOp",EDGE,"E18"),sQuery(id+"F0.wireOp",EDGE,"E19"),sQuery(id+"F0.wireOp",EDGE,"E20"),sQuery(id+"F0.wireOp",EDGE,"E21"),sQuery(id+"F0.wireOp",EDGE,"E22"),sQuery(id+"F0.wireOp",EDGE,"E23"),sQuery(id+"F0.wireOp",EDGE,"E24"),sQuery(id+"F0.wireOp",EDGE,"E25"),sQuery(id+"F0.wireOp",EDGE,"E26"),sQuery(id+"F0.wireOp",EDGE,"E27"),sQuery(id+"F0.wireOp",EDGE,"E28"),sQuery(id+"F0.wireOp",EDGE,"E29")])],"isStart":false})]});}
            var Q10;
            {var subQ0=sQuery(id+"F0.wireOp",EDGE,"E24");Q10=makeQuery(id+"F2.opChamfer","BLEND_EDGE",EDGE,{"blendedFrom":[makeQuery(id+"F1.opExtrude","CAP_EDGE",EDGE,{"disambiguationData":[OSD([subQ0])],"isStart":true}),makeQuery(id+"F1.opExtrude","CAP_FACE",FACE,{"disambiguationData":[OSD([sQuery(id+"F0.wireOp",EDGE,"E0"),sQuery(id+"F0.wireOp",EDGE,"E1"),sQuery(id+"F0.wireOp",EDGE,"E2"),sQuery(id+"F0.wireOp",EDGE,"E4"),sQuery(id+"F0.wireOp",EDGE,"E5"),sQuery(id+"F0.wireOp",EDGE,"E7"),sQuery(id+"F0.wireOp",EDGE,"E8"),sQuery(id+"F0.wireOp",EDGE,"E10"),sQuery(id+"F0.wireOp",EDGE,"E11"),sQuery(id+"F0.wireOp",EDGE,"E13"),sQuery(id+"F0.wireOp",EDGE,"E14"),sQuery(id+"F0.wireOp",EDGE,"E15"),sQuery(id+"F0.wireOp",EDGE,"E16"),sQuery(id+"F0.wireOp",EDGE,"E17"),sQuery(id+"F0.wireOp",EDGE,"E18"),sQuery(id+"F0.wireOp",EDGE,"E19"),sQuery(id+"F0.wireOp",EDGE,"E20"),sQuery(id+"F0.wireOp",EDGE,"E21"),sQuery(id+"F0.wireOp",EDGE,"E22"),sQuery(id+"F0.wireOp",EDGE,"E23"),subQ0,sQuery(id+"F0.wireOp",EDGE,"E25"),sQuery(id+"F0.wireOp",EDGE,"E26"),sQuery(id+"F0.wireOp",EDGE,"E27"),sQuery(id+"F0.wireOp",EDGE,"E28"),sQuery(id+"F0.wireOp",EDGE,"E29")])],"isStart":true})],"blendedInto":[makeQuery(id+"F1.opExtrude","CAP_FACE",FACE,{"disambiguationData":[OSD([sQuery(id+"F0.wireOp",EDGE,"E0"),sQuery(id+"F0.wireOp",EDGE,"E1"),sQuery(id+"F0.wireOp",EDGE,"E2"),sQuery(id+"F0.wireOp",EDGE,"E4"),sQuery(id+"F0.wireOp",EDGE,"E5"),sQuery(id+"F0.wireOp",EDGE,"E7"),sQuery(id+"F0.wireOp",EDGE,"E8"),sQuery(id+"F0.wireOp",EDGE,"E10"),sQuery(id+"F0.wireOp",EDGE,"E11"),sQuery(id+"F0.wireOp",EDGE,"E13"),sQuery(id+"F0.wireOp",EDGE,"E14"),sQuery(id+"F0.wireOp",EDGE,"E15"),sQuery(id+"F0.wireOp",EDGE,"E16"),sQuery(id+"F0.wireOp",EDGE,"E17"),sQuery(id+"F0.wireOp",EDGE,"E18"),sQuery(id+"F0.wireOp",EDGE,"E19"),sQuery(id+"F0.wireOp",EDGE,"E20"),sQuery(id+"F0.wireOp",EDGE,"E21"),sQuery(id+"F0.wireOp",EDGE,"E22"),sQuery(id+"F0.wireOp",EDGE,"E23"),subQ0,sQuery(id+"F0.wireOp",EDGE,"E25"),sQuery(id+"F0.wireOp",EDGE,"E26"),sQuery(id+"F0.wireOp",EDGE,"E27"),sQuery(id+"F0.wireOp",EDGE,"E28"),sQuery(id+"F0.wireOp",EDGE,"E29")])],"isStart":true})]});}
            var Q11;
            {var subQ0=sQuery(id+"F0.wireOp",EDGE,"E23");Q11=makeQuery(id+"F2.opChamfer","BLEND_EDGE",EDGE,{"blendedFrom":[makeQuery(id+"F1.opExtrude","CAP_EDGE",EDGE,{"disambiguationData":[OSD([subQ0])],"isStart":true}),makeQuery(id+"F1.opExtrude","CAP_FACE",FACE,{"disambiguationData":[OSD([sQuery(id+"F0.wireOp",EDGE,"E0"),sQuery(id+"F0.wireOp",EDGE,"E1"),sQuery(id+"F0.wireOp",EDGE,"E2"),sQuery(id+"F0.wireOp",EDGE,"E4"),sQuery(id+"F0.wireOp",EDGE,"E5"),sQuery(id+"F0.wireOp",EDGE,"E7"),sQuery(id+"F0.wireOp",EDGE,"E8"),sQuery(id+"F0.wireOp",EDGE,"E10"),sQuery(id+"F0.wireOp",EDGE,"E11"),sQuery(id+"F0.wireOp",EDGE,"E13"),sQuery(id+"F0.wireOp",EDGE,"E14"),sQuery(id+"F0.wireOp",EDGE,"E15"),sQuery(id+"F0.wireOp",EDGE,"E16"),sQuery(id+"F0.wireOp",EDGE,"E17"),sQuery(id+"F0.wireOp",EDGE,"E18"),sQuery(id+"F0.wireOp",EDGE,"E19"),sQuery(id+"F0.wireOp",EDGE,"E20"),sQuery(id+"F0.wireOp",EDGE,"E21"),sQuery(id+"F0.wireOp",EDGE,"E22"),subQ0,sQuery(id+"F0.wireOp",EDGE,"E24"),sQuery(id+"F0.wireOp",EDGE,"E25"),sQuery(id+"F0.wireOp",EDGE,"E26"),sQuery(id+"F0.wireOp",EDGE,"E27"),sQuery(id+"F0.wireOp",EDGE,"E28"),sQuery(id+"F0.wireOp",EDGE,"E29")])],"isStart":true})],"blendedInto":[makeQuery(id+"F1.opExtrude","CAP_FACE",FACE,{"disambiguationData":[OSD([sQuery(id+"F0.wireOp",EDGE,"E0"),sQuery(id+"F0.wireOp",EDGE,"E1"),sQuery(id+"F0.wireOp",EDGE,"E2"),sQuery(id+"F0.wireOp",EDGE,"E4"),sQuery(id+"F0.wireOp",EDGE,"E5"),sQuery(id+"F0.wireOp",EDGE,"E7"),sQuery(id+"F0.wireOp",EDGE,"E8"),sQuery(id+"F0.wireOp",EDGE,"E10"),sQuery(id+"F0.wireOp",EDGE,"E11"),sQuery(id+"F0.wireOp",EDGE,"E13"),sQuery(id+"F0.wireOp",EDGE,"E14"),sQuery(id+"F0.wireOp",EDGE,"E15"),sQuery(id+"F0.wireOp",EDGE,"E16"),sQuery(id+"F0.wireOp",EDGE,"E17"),sQuery(id+"F0.wireOp",EDGE,"E18"),sQuery(id+"F0.wireOp",EDGE,"E19"),sQuery(id+"F0.wireOp",EDGE,"E20"),sQuery(id+"F0.wireOp",EDGE,"E21"),sQuery(id+"F0.wireOp",EDGE,"E22"),subQ0,sQuery(id+"F0.wireOp",EDGE,"E24"),sQuery(id+"F0.wireOp",EDGE,"E25"),sQuery(id+"F0.wireOp",EDGE,"E26"),sQuery(id+"F0.wireOp",EDGE,"E27"),sQuery(id+"F0.wireOp",EDGE,"E28"),sQuery(id+"F0.wireOp",EDGE,"E29")])],"isStart":true})]});}
            var Q12;
            {var subQ0=sQuery(id+"F0.wireOp",EDGE,"E20");Q12=makeQuery(id+"F2.opChamfer","BLEND_EDGE",EDGE,{"blendedFrom":[makeQuery(id+"F1.opExtrude","CAP_EDGE",EDGE,{"disambiguationData":[OSD([subQ0])],"isStart":true}),makeQuery(id+"F1.opExtrude","CAP_FACE",FACE,{"disambiguationData":[OSD([sQuery(id+"F0.wireOp",EDGE,"E0"),sQuery(id+"F0.wireOp",EDGE,"E1"),sQuery(id+"F0.wireOp",EDGE,"E2"),sQuery(id+"F0.wireOp",EDGE,"E4"),sQuery(id+"F0.wireOp",EDGE,"E5"),sQuery(id+"F0.wireOp",EDGE,"E7"),sQuery(id+"F0.wireOp",EDGE,"E8"),sQuery(id+"F0.wireOp",EDGE,"E10"),sQuery(id+"F0.wireOp",EDGE,"E11"),sQuery(id+"F0.wireOp",EDGE,"E13"),sQuery(id+"F0.wireOp",EDGE,"E14"),sQuery(id+"F0.wireOp",EDGE,"E15"),sQuery(id+"F0.wireOp",EDGE,"E16"),sQuery(id+"F0.wireOp",EDGE,"E17"),sQuery(id+"F0.wireOp",EDGE,"E18"),sQuery(id+"F0.wireOp",EDGE,"E19"),subQ0,sQuery(id+"F0.wireOp",EDGE,"E21"),sQuery(id+"F0.wireOp",EDGE,"E22"),sQuery(id+"F0.wireOp",EDGE,"E23"),sQuery(id+"F0.wireOp",EDGE,"E24"),sQuery(id+"F0.wireOp",EDGE,"E25"),sQuery(id+"F0.wireOp",EDGE,"E26"),sQuery(id+"F0.wireOp",EDGE,"E27"),sQuery(id+"F0.wireOp",EDGE,"E28"),sQuery(id+"F0.wireOp",EDGE,"E29")])],"isStart":true})],"blendedInto":[makeQuery(id+"F1.opExtrude","CAP_FACE",FACE,{"disambiguationData":[OSD([sQuery(id+"F0.wireOp",EDGE,"E0"),sQuery(id+"F0.wireOp",EDGE,"E1"),sQuery(id+"F0.wireOp",EDGE,"E2"),sQuery(id+"F0.wireOp",EDGE,"E4"),sQuery(id+"F0.wireOp",EDGE,"E5"),sQuery(id+"F0.wireOp",EDGE,"E7"),sQuery(id+"F0.wireOp",EDGE,"E8"),sQuery(id+"F0.wireOp",EDGE,"E10"),sQuery(id+"F0.wireOp",EDGE,"E11"),sQuery(id+"F0.wireOp",EDGE,"E13"),sQuery(id+"F0.wireOp",EDGE,"E14"),sQuery(id+"F0.wireOp",EDGE,"E15"),sQuery(id+"F0.wireOp",EDGE,"E16"),sQuery(id+"F0.wireOp",EDGE,"E17"),sQuery(id+"F0.wireOp",EDGE,"E18"),sQuery(id+"F0.wireOp",EDGE,"E19"),subQ0,sQuery(id+"F0.wireOp",EDGE,"E21"),sQuery(id+"F0.wireOp",EDGE,"E22"),sQuery(id+"F0.wireOp",EDGE,"E23"),sQuery(id+"F0.wireOp",EDGE,"E24"),sQuery(id+"F0.wireOp",EDGE,"E25"),sQuery(id+"F0.wireOp",EDGE,"E26"),sQuery(id+"F0.wireOp",EDGE,"E27"),sQuery(id+"F0.wireOp",EDGE,"E28"),sQuery(id+"F0.wireOp",EDGE,"E29")])],"isStart":true})]});}
            var Q13;
            {var subQ0=sQuery(id+"F0.wireOp",EDGE,"E19");Q13=makeQuery(id+"F2.opChamfer","BLEND_EDGE",EDGE,{"blendedFrom":[makeQuery(id+"F1.opExtrude","CAP_EDGE",EDGE,{"disambiguationData":[OSD([subQ0])],"isStart":true}),makeQuery(id+"F1.opExtrude","CAP_FACE",FACE,{"disambiguationData":[OSD([sQuery(id+"F0.wireOp",EDGE,"E0"),sQuery(id+"F0.wireOp",EDGE,"E1"),sQuery(id+"F0.wireOp",EDGE,"E2"),sQuery(id+"F0.wireOp",EDGE,"E4"),sQuery(id+"F0.wireOp",EDGE,"E5"),sQuery(id+"F0.wireOp",EDGE,"E7"),sQuery(id+"F0.wireOp",EDGE,"E8"),sQuery(id+"F0.wireOp",EDGE,"E10"),sQuery(id+"F0.wireOp",EDGE,"E11"),sQuery(id+"F0.wireOp",EDGE,"E13"),sQuery(id+"F0.wireOp",EDGE,"E14"),sQuery(id+"F0.wireOp",EDGE,"E15"),sQuery(id+"F0.wireOp",EDGE,"E16"),sQuery(id+"F0.wireOp",EDGE,"E17"),sQuery(id+"F0.wireOp",EDGE,"E18"),subQ0,sQuery(id+"F0.wireOp",EDGE,"E20"),sQuery(id+"F0.wireOp",EDGE,"E21"),sQuery(id+"F0.wireOp",EDGE,"E22"),sQuery(id+"F0.wireOp",EDGE,"E23"),sQuery(id+"F0.wireOp",EDGE,"E24"),sQuery(id+"F0.wireOp",EDGE,"E25"),sQuery(id+"F0.wireOp",EDGE,"E26"),sQuery(id+"F0.wireOp",EDGE,"E27"),sQuery(id+"F0.wireOp",EDGE,"E28"),sQuery(id+"F0.wireOp",EDGE,"E29")])],"isStart":true})],"blendedInto":[makeQuery(id+"F1.opExtrude","CAP_FACE",FACE,{"disambiguationData":[OSD([sQuery(id+"F0.wireOp",EDGE,"E0"),sQuery(id+"F0.wireOp",EDGE,"E1"),sQuery(id+"F0.wireOp",EDGE,"E2"),sQuery(id+"F0.wireOp",EDGE,"E4"),sQuery(id+"F0.wireOp",EDGE,"E5"),sQuery(id+"F0.wireOp",EDGE,"E7"),sQuery(id+"F0.wireOp",EDGE,"E8"),sQuery(id+"F0.wireOp",EDGE,"E10"),sQuery(id+"F0.wireOp",EDGE,"E11"),sQuery(id+"F0.wireOp",EDGE,"E13"),sQuery(id+"F0.wireOp",EDGE,"E14"),sQuery(id+"F0.wireOp",EDGE,"E15"),sQuery(id+"F0.wireOp",EDGE,"E16"),sQuery(id+"F0.wireOp",EDGE,"E17"),sQuery(id+"F0.wireOp",EDGE,"E18"),subQ0,sQuery(id+"F0.wireOp",EDGE,"E20"),sQuery(id+"F0.wireOp",EDGE,"E21"),sQuery(id+"F0.wireOp",EDGE,"E22"),sQuery(id+"F0.wireOp",EDGE,"E23"),sQuery(id+"F0.wireOp",EDGE,"E24"),sQuery(id+"F0.wireOp",EDGE,"E25"),sQuery(id+"F0.wireOp",EDGE,"E26"),sQuery(id+"F0.wireOp",EDGE,"E27"),sQuery(id+"F0.wireOp",EDGE,"E28"),sQuery(id+"F0.wireOp",EDGE,"E29")])],"isStart":true})]});}
            var Q14;
            {var subQ0=sQuery(id+"F0.wireOp",EDGE,"E15");Q14=makeQuery(id+"F2.opChamfer","BLEND_EDGE",EDGE,{"blendedFrom":[makeQuery(id+"F1.opExtrude","CAP_EDGE",EDGE,{"disambiguationData":[OSD([subQ0])],"isStart":true}),makeQuery(id+"F1.opExtrude","CAP_FACE",FACE,{"disambiguationData":[OSD([sQuery(id+"F0.wireOp",EDGE,"E0"),sQuery(id+"F0.wireOp",EDGE,"E1"),sQuery(id+"F0.wireOp",EDGE,"E2"),sQuery(id+"F0.wireOp",EDGE,"E4"),sQuery(id+"F0.wireOp",EDGE,"E5"),sQuery(id+"F0.wireOp",EDGE,"E7"),sQuery(id+"F0.wireOp",EDGE,"E8"),sQuery(id+"F0.wireOp",EDGE,"E10"),sQuery(id+"F0.wireOp",EDGE,"E11"),sQuery(id+"F0.wireOp",EDGE,"E13"),sQuery(id+"F0.wireOp",EDGE,"E14"),subQ0,sQuery(id+"F0.wireOp",EDGE,"E16"),sQuery(id+"F0.wireOp",EDGE,"E17"),sQuery(id+"F0.wireOp",EDGE,"E18"),sQuery(id+"F0.wireOp",EDGE,"E19"),sQuery(id+"F0.wireOp",EDGE,"E20"),sQuery(id+"F0.wireOp",EDGE,"E21"),sQuery(id+"F0.wireOp",EDGE,"E22"),sQuery(id+"F0.wireOp",EDGE,"E23"),sQuery(id+"F0.wireOp",EDGE,"E24"),sQuery(id+"F0.wireOp",EDGE,"E25"),sQuery(id+"F0.wireOp",EDGE,"E26"),sQuery(id+"F0.wireOp",EDGE,"E27"),sQuery(id+"F0.wireOp",EDGE,"E28"),sQuery(id+"F0.wireOp",EDGE,"E29")])],"isStart":true})],"blendedInto":[makeQuery(id+"F1.opExtrude","CAP_FACE",FACE,{"disambiguationData":[OSD([sQuery(id+"F0.wireOp",EDGE,"E0"),sQuery(id+"F0.wireOp",EDGE,"E1"),sQuery(id+"F0.wireOp",EDGE,"E2"),sQuery(id+"F0.wireOp",EDGE,"E4"),sQuery(id+"F0.wireOp",EDGE,"E5"),sQuery(id+"F0.wireOp",EDGE,"E7"),sQuery(id+"F0.wireOp",EDGE,"E8"),sQuery(id+"F0.wireOp",EDGE,"E10"),sQuery(id+"F0.wireOp",EDGE,"E11"),sQuery(id+"F0.wireOp",EDGE,"E13"),sQuery(id+"F0.wireOp",EDGE,"E14"),subQ0,sQuery(id+"F0.wireOp",EDGE,"E16"),sQuery(id+"F0.wireOp",EDGE,"E17"),sQuery(id+"F0.wireOp",EDGE,"E18"),sQuery(id+"F0.wireOp",EDGE,"E19"),sQuery(id+"F0.wireOp",EDGE,"E20"),sQuery(id+"F0.wireOp",EDGE,"E21"),sQuery(id+"F0.wireOp",EDGE,"E22"),sQuery(id+"F0.wireOp",EDGE,"E23"),sQuery(id+"F0.wireOp",EDGE,"E24"),sQuery(id+"F0.wireOp",EDGE,"E25"),sQuery(id+"F0.wireOp",EDGE,"E26"),sQuery(id+"F0.wireOp",EDGE,"E27"),sQuery(id+"F0.wireOp",EDGE,"E28"),sQuery(id+"F0.wireOp",EDGE,"E29")])],"isStart":true})]});}
            var Q15;
            {var subQ0=sQuery(id+"F0.wireOp",EDGE,"E16");Q15=makeQuery(id+"F2.opChamfer","BLEND_EDGE",EDGE,{"blendedFrom":[makeQuery(id+"F1.opExtrude","CAP_EDGE",EDGE,{"disambiguationData":[OSD([subQ0])],"isStart":true}),makeQuery(id+"F1.opExtrude","CAP_FACE",FACE,{"disambiguationData":[OSD([sQuery(id+"F0.wireOp",EDGE,"E0"),sQuery(id+"F0.wireOp",EDGE,"E1"),sQuery(id+"F0.wireOp",EDGE,"E2"),sQuery(id+"F0.wireOp",EDGE,"E4"),sQuery(id+"F0.wireOp",EDGE,"E5"),sQuery(id+"F0.wireOp",EDGE,"E7"),sQuery(id+"F0.wireOp",EDGE,"E8"),sQuery(id+"F0.wireOp",EDGE,"E10"),sQuery(id+"F0.wireOp",EDGE,"E11"),sQuery(id+"F0.wireOp",EDGE,"E13"),sQuery(id+"F0.wireOp",EDGE,"E14"),sQuery(id+"F0.wireOp",EDGE,"E15"),subQ0,sQuery(id+"F0.wireOp",EDGE,"E17"),sQuery(id+"F0.wireOp",EDGE,"E18"),sQuery(id+"F0.wireOp",EDGE,"E19"),sQuery(id+"F0.wireOp",EDGE,"E20"),sQuery(id+"F0.wireOp",EDGE,"E21"),sQuery(id+"F0.wireOp",EDGE,"E22"),sQuery(id+"F0.wireOp",EDGE,"E23"),sQuery(id+"F0.wireOp",EDGE,"E24"),sQuery(id+"F0.wireOp",EDGE,"E25"),sQuery(id+"F0.wireOp",EDGE,"E26"),sQuery(id+"F0.wireOp",EDGE,"E27"),sQuery(id+"F0.wireOp",EDGE,"E28"),sQuery(id+"F0.wireOp",EDGE,"E29")])],"isStart":true})],"blendedInto":[makeQuery(id+"F1.opExtrude","CAP_FACE",FACE,{"disambiguationData":[OSD([sQuery(id+"F0.wireOp",EDGE,"E0"),sQuery(id+"F0.wireOp",EDGE,"E1"),sQuery(id+"F0.wireOp",EDGE,"E2"),sQuery(id+"F0.wireOp",EDGE,"E4"),sQuery(id+"F0.wireOp",EDGE,"E5"),sQuery(id+"F0.wireOp",EDGE,"E7"),sQuery(id+"F0.wireOp",EDGE,"E8"),sQuery(id+"F0.wireOp",EDGE,"E10"),sQuery(id+"F0.wireOp",EDGE,"E11"),sQuery(id+"F0.wireOp",EDGE,"E13"),sQuery(id+"F0.wireOp",EDGE,"E14"),sQuery(id+"F0.wireOp",EDGE,"E15"),subQ0,sQuery(id+"F0.wireOp",EDGE,"E17"),sQuery(id+"F0.wireOp",EDGE,"E18"),sQuery(id+"F0.wireOp",EDGE,"E19"),sQuery(id+"F0.wireOp",EDGE,"E20"),sQuery(id+"F0.wireOp",EDGE,"E21"),sQuery(id+"F0.wireOp",EDGE,"E22"),sQuery(id+"F0.wireOp",EDGE,"E23"),sQuery(id+"F0.wireOp",EDGE,"E24"),sQuery(id+"F0.wireOp",EDGE,"E25"),sQuery(id+"F0.wireOp",EDGE,"E26"),sQuery(id+"F0.wireOp",EDGE,"E27"),sQuery(id+"F0.wireOp",EDGE,"E28"),sQuery(id+"F0.wireOp",EDGE,"E29")])],"isStart":true})]});}
            chamfer(context, id + "F3", {"entities" : qUnion([Q0, Q1, Q2, Q3, Q4, Q5, Q6, Q7, Q8, Q9, Q10, Q11, Q12, Q13, Q14, Q15]), "width" : 2.85 * mm, "tangentPropagation" : true});
        }
    });
